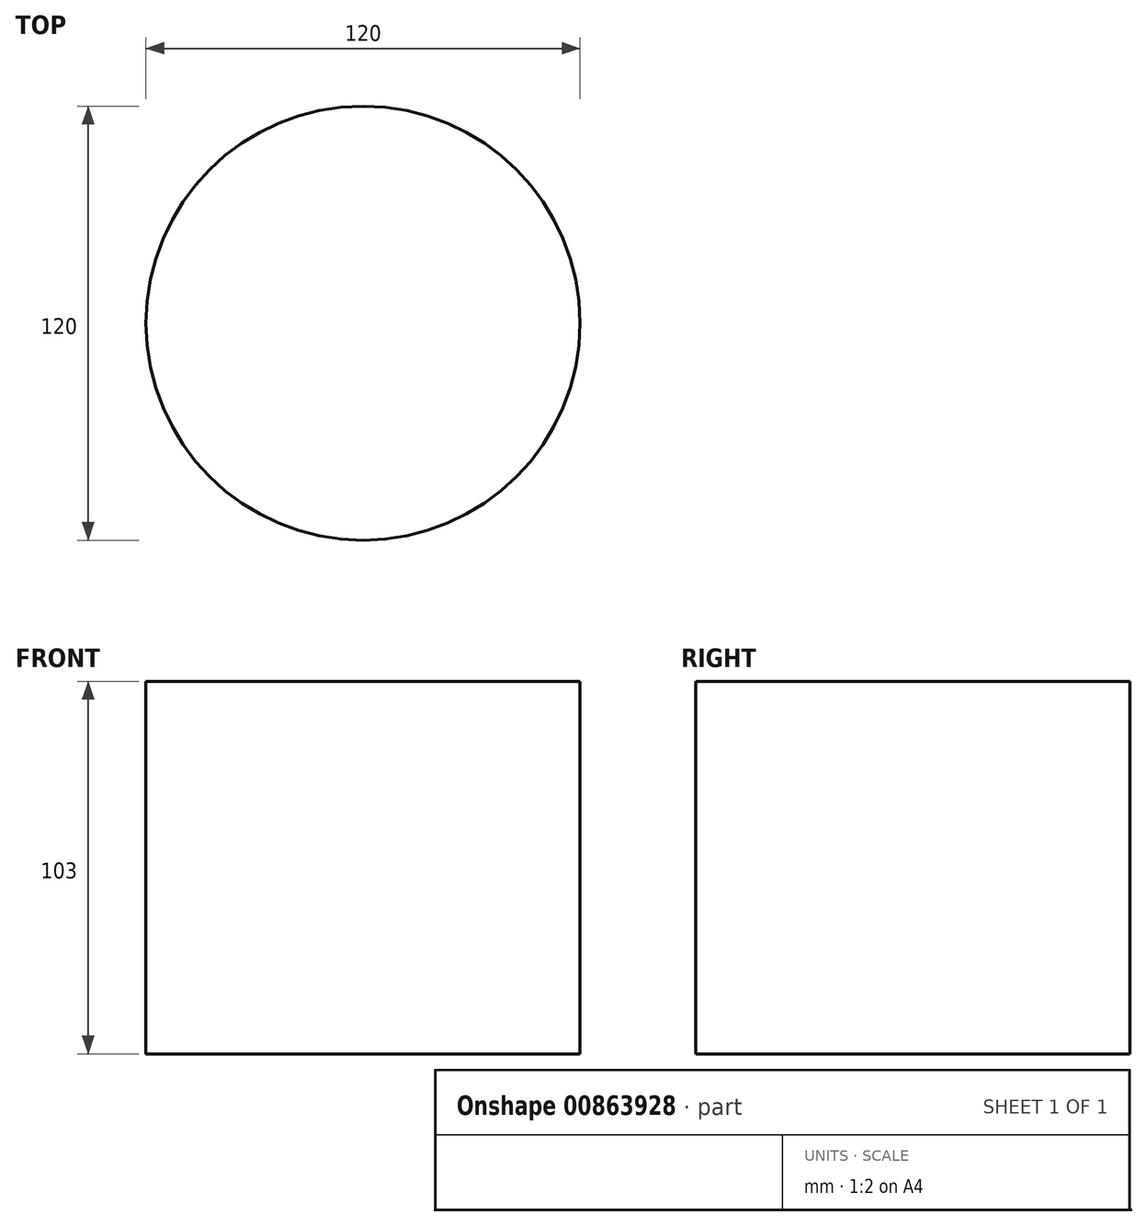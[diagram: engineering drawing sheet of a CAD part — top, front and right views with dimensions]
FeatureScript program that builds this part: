
annotation { "Feature Type Name" : "Feature", "Feature Type Description" : "" }
export const myFeature = defineFeature(function(context is Context, id is Id, definition is map)
    precondition{}
    {
        {
            var Q0;
            Q0=qCreatedBy(makeId("Top.planeOp"),FACE);
            var sketch = newSketch(context, id + "F0", { "sketchPlane" : qUnion([Q0])});
            skCircle(sketch, "E0", {"center": v(0, 0) * mm, "radius": 60 * mm});
            skSolve(sketch);
        }
        {
            var Q0;
            Q0=makeQuery(id+"F0.imprint","IMPRINT",FACE,{"disambiguationData":[TD([[makeQuery(id+"F0.imprint","IMPRINT",EDGE,{"derivedFrom":sQuery(id+"F0.wireOp",EDGE,"E0")}),1.0]])]});
            extrude(context, id + "F1", {"entities" : qUnion([Q0]), "depth" : 103 * mm, "offsetDistance" : 25 * mm});
        }
    });
